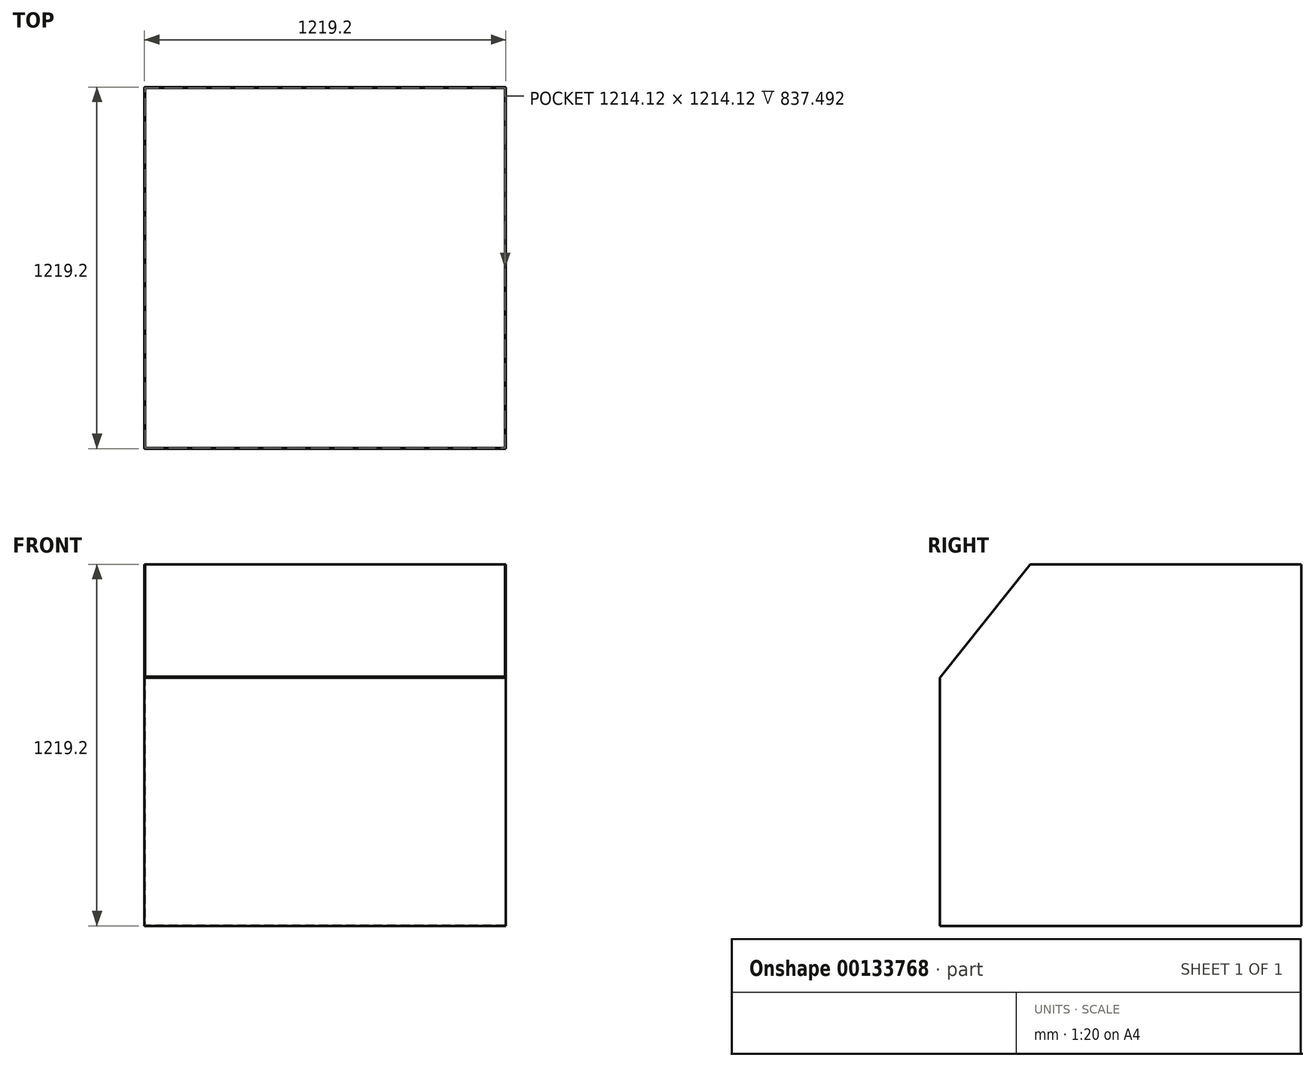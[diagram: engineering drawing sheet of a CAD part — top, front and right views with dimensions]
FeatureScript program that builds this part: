
annotation { "Feature Type Name" : "Feature", "Feature Type Description" : "" }
export const myFeature = defineFeature(function(context is Context, id is Id, definition is map)
    precondition{}
    {
        {
            var Q0;
            Q0=qCreatedBy(makeId("Top.planeOp"),FACE);
            var sketch = newSketch(context, id + "F0", { "sketchPlane" : qUnion([Q0])});
            skLineSegment(sketch, "E0.bottom", {"start": v(609.6, -609.6) * mm, "end": v(-609.6, -609.6) * mm});
            skLineSegment(sketch, "E0.top", {"start": v(609.6, 609.6) * mm, "end": v(-609.6, 609.6) * mm});
            skLineSegment(sketch, "E0.left", {"start": v(609.6, -609.6) * mm, "end": v(609.6, 609.6) * mm});
            skLineSegment(sketch, "E0.right", {"start": v(-609.6, -609.6) * mm, "end": v(-609.6, 609.6) * mm});
            skPoint(sketch, "E0.middle", {"position": v(0, 0) * mm});
            skSolve(sketch);
        }
        {
            var Q0;
            Q0=makeQuery(id+"F0.imprint","IMPRINT",FACE,{"disambiguationData":[TD([[makeQuery(id+"F0.imprint","IMPRINT",EDGE,{"derivedFrom":sQuery(id+"F0.wireOp",EDGE,"E0.bottom")}),-1.0]])]});
            extrude(context, id + "F1", {"entities" : qUnion([Q0]), "depth" : 1219.2 * mm});
        }
        {
            var Q0;
            Q0=makeQuery(id+"F1.opExtrude","CAP_FACE",FACE,{"disambiguationData":[OSD([sQuery(id+"F0.wireOp",EDGE,"E0.bottom"),sQuery(id+"F0.wireOp",EDGE,"E0.top"),sQuery(id+"F0.wireOp",EDGE,"E0.left"),sQuery(id+"F0.wireOp",EDGE,"E0.right")])],"isStart":false});
            shell(context, id + "F2", {"entities" : qUnion([Q0]), "thickness" : 2.54 * mm});
        }
        {
            var Q0;
            Q0=makeQuery(id+"F1.opExtrude","SWEPT_FACE",FACE,{"disambiguationData":[OSD([sQuery(id+"F0.wireOp",EDGE,"E0.right")])]});
            var sketch = newSketch(context, id + "F3", { "sketchPlane" : qUnion([Q0])});
            skLineSegment(sketch, "E1", {"start": v(609.6, 1219.2) * mm, "end": v(304.8, 1219.2) * mm});
            skLineSegment(sketch, "E2", {"start": v(304.8, 1219.2) * mm, "end": v(609.6, 836.85) * mm});
            skLineSegment(sketch, "E3", {"start": v(609.6, 836.85) * mm, "end": v(609.6, 1219.2) * mm});
            skSolve(sketch);
        }
        {
            var Q0;
            Q0=makeQuery(id+"F3.imprint","IMPRINT",FACE,{"disambiguationData":[TD([[makeQuery(id+"F3.imprint","IMPRINT",EDGE,{"derivedFrom":sQuery(id+"F3.wireOp",EDGE,"E1")}),1.0]])]});
            extrude(context, id + "F4", {"entities" : qUnion([Q0]), "operationType" : NewBodyOperationType.REMOVE, "oppositeDirection" : true, "depth" : 1219.2 * mm});
        }
    });
